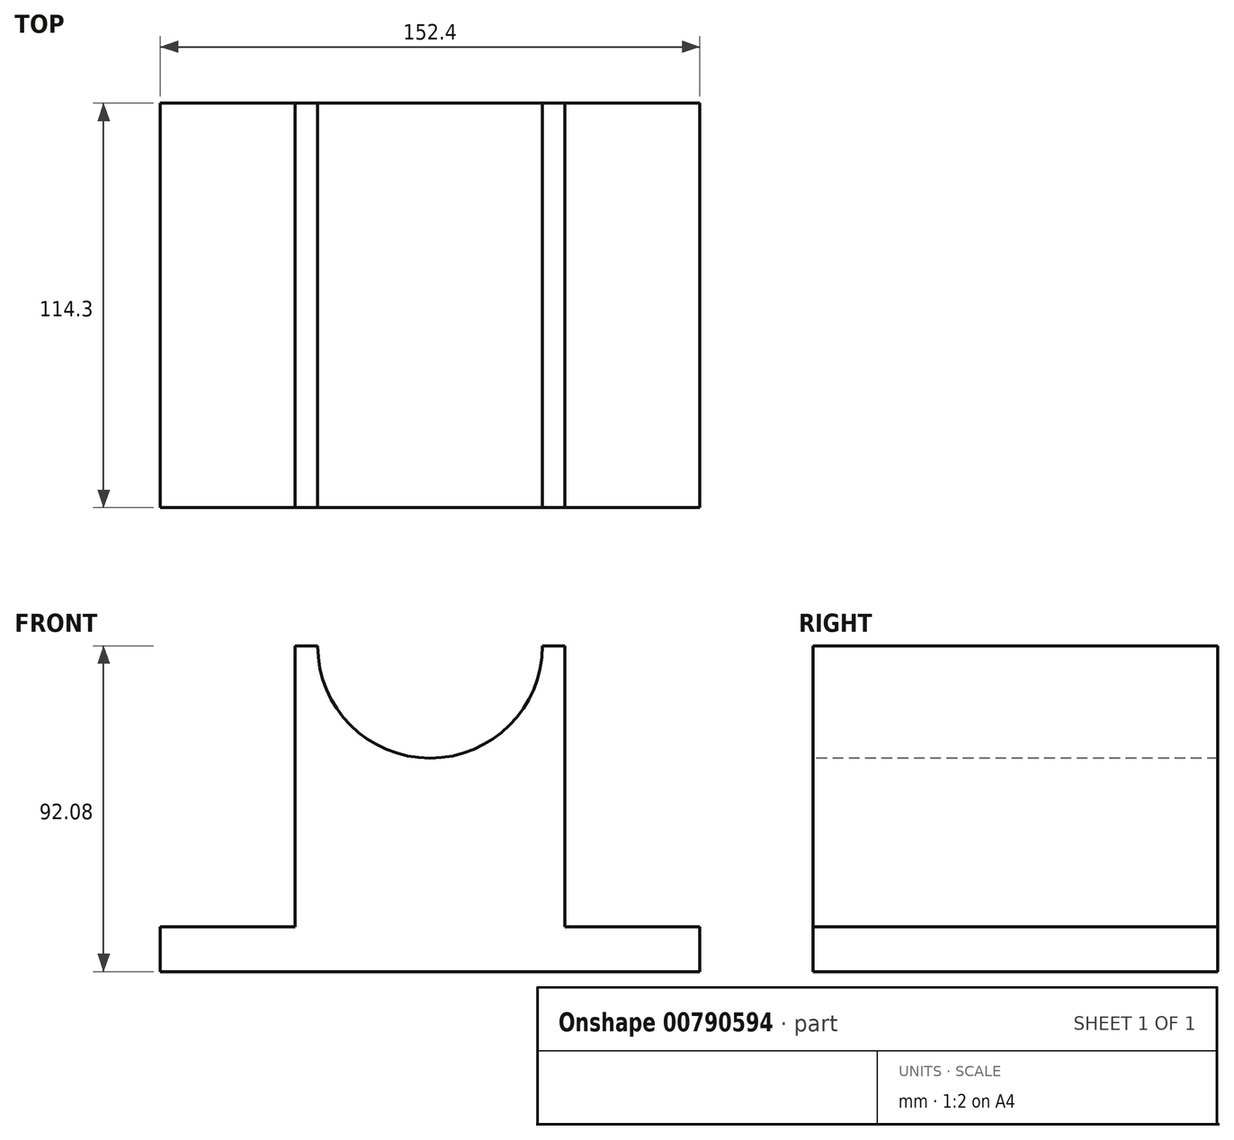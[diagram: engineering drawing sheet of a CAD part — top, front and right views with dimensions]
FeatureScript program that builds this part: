
annotation { "Feature Type Name" : "Feature", "Feature Type Description" : "" }
export const myFeature = defineFeature(function(context is Context, id is Id, definition is map)
    precondition{}
    {
        {
            var Q0;
            Q0=qCreatedBy(makeId("Front.planeOp"),FACE);
            var sketch = newSketch(context, id + "F0", { "sketchPlane" : qUnion([Q0])});
            skLineSegment(sketch, "E0", {"start": v(0, 0) * mm, "end": v(0, 12.7) * mm});
            skLineSegment(sketch, "E1", {"start": v(0, 12.7) * mm, "end": v(38.1, 12.7) * mm});
            skLineSegment(sketch, "E2", {"start": v(38.1, 12.7) * mm, "end": v(38.1, 92.08) * mm});
            skLineSegment(sketch, "E3", {"start": v(38.1, 92.08) * mm, "end": v(114.3, 92.08) * mm});
            skLineSegment(sketch, "E4", {"start": v(114.3, 92.08) * mm, "end": v(114.3, 12.7) * mm});
            skLineSegment(sketch, "E5", {"start": v(114.3, 12.7) * mm, "end": v(152.4, 12.7) * mm});
            skLineSegment(sketch, "E6", {"start": v(152.4, 12.7) * mm, "end": v(152.4, 0) * mm});
            skLineSegment(sketch, "E7", {"start": v(152.4, 0) * mm, "end": v(0, 0) * mm});
            skSolve(sketch);
        }
        {
            var Q0;
            Q0=makeQuery(id+"F0.imprint","IMPRINT",FACE,{"disambiguationData":[TD([[makeQuery(id+"F0.imprint","IMPRINT",EDGE,{"derivedFrom":sQuery(id+"F0.wireOp",EDGE,"E0")}),-1.0]])]});
            extrude(context, id + "F1", {"entities" : qUnion([Q0]), "depth" : 114.3 * mm, "offsetDistance" : 25.4 * mm});
        }
        {
            var Q0;
            Q0=makeQuery(id+"F1.opExtrude","CAP_FACE",FACE,{"disambiguationData":[OSD([sQuery(id+"F0.wireOp",EDGE,"E0"),sQuery(id+"F0.wireOp",EDGE,"E1"),sQuery(id+"F0.wireOp",EDGE,"E2"),sQuery(id+"F0.wireOp",EDGE,"E3"),sQuery(id+"F0.wireOp",EDGE,"E4"),sQuery(id+"F0.wireOp",EDGE,"E5"),sQuery(id+"F0.wireOp",EDGE,"E6"),sQuery(id+"F0.wireOp",EDGE,"E7")])],"isStart":false});
            var sketch = newSketch(context, id + "F2", { "sketchPlane" : qUnion([Q0])});
            skCircle(sketch, "E8", {"center": v(76.2, 92.08) * mm, "radius": 31.75 * mm});
            skSolve(sketch);
        }
        {
            var Q0;
            Q0 = qSketchRegion(id + "F2", true);
            extrude(context, id + "F3", {"entities" : qUnion([Q0]), "operationType" : NewBodyOperationType.REMOVE, "endBound" : BoundingType.THROUGH_ALL, "oppositeDirection" : true, "depth" : 25.4 * mm, "offsetDistance" : 25.4 * mm});
        }
    });
